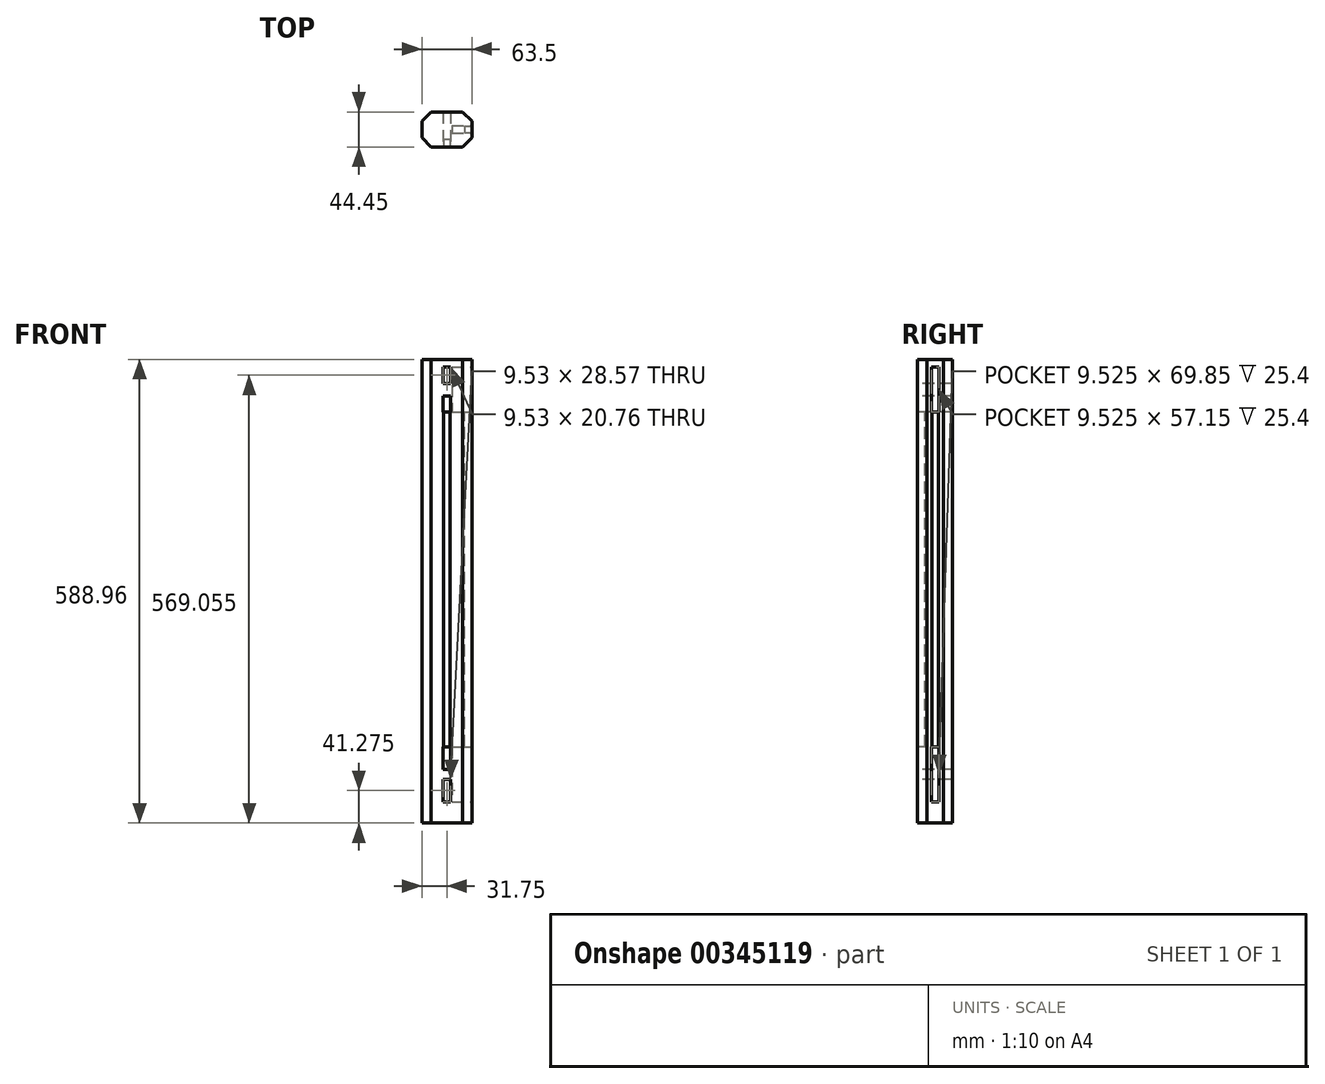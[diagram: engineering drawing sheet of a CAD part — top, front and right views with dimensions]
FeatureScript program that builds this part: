
annotation { "Feature Type Name" : "Feature", "Feature Type Description" : "" }
export const myFeature = defineFeature(function(context is Context, id is Id, definition is map)
    precondition{}
    {
        {
            var Q0;
            Q0=qCreatedBy(makeId("Top.planeOp"),FACE);
            var sketch = newSketch(context, id + "F0", { "sketchPlane" : qUnion([Q0])});
            skLineSegment(sketch, "E0", {"start": v(0, 0) * mm, "end": v(63.5, 0) * mm});
            skLineSegment(sketch, "E1", {"start": v(63.5, 0) * mm, "end": v(63.5, 44.45) * mm});
            skLineSegment(sketch, "E2", {"start": v(63.5, 44.45) * mm, "end": v(0, 44.45) * mm});
            skLineSegment(sketch, "E3", {"start": v(0, 44.45) * mm, "end": v(0, 0) * mm});
            skSolve(sketch);
        }
        {
            var Q0;
            Q0=qSketchRegion(id+"F0",true);
            extrude(context, id + "F1", {"entities" : qUnion([Q0]), "depth" : 588.96 * mm});
        }
        {
            var Q0;
            Q0=makeQuery(id+"F1.opExtrude","SWEPT_FACE",FACE,{"disambiguationData":[OSD([sQuery(id+"F0.wireOp",EDGE,"E1")])]});
            var sketch = newSketch(context, id + "F2", { "sketchPlane" : qUnion([Q0])});
            skLineSegment(sketch, "E4", {"start": v(17.46, 579.44) * mm, "end": v(17.46, 522.29) * mm});
            skLineSegment(sketch, "E5", {"start": v(17.46, 522.29) * mm, "end": v(26.99, 522.29) * mm});
            skLineSegment(sketch, "E6", {"start": v(26.99, 522.29) * mm, "end": v(26.99, 579.44) * mm});
            skLineSegment(sketch, "E7", {"start": v(26.99, 579.44) * mm, "end": v(17.46, 579.44) * mm});
            skLineSegment(sketch, "E8", {"start": v(17.46, 96.84) * mm, "end": v(17.46, 26.99) * mm});
            skLineSegment(sketch, "E9", {"start": v(17.46, 26.99) * mm, "end": v(26.99, 26.99) * mm});
            skLineSegment(sketch, "E10", {"start": v(26.99, 26.99) * mm, "end": v(26.99, 96.84) * mm});
            skLineSegment(sketch, "E11", {"start": v(26.99, 96.84) * mm, "end": v(17.46, 96.84) * mm});
            skPoint(sketch, "E12", {"position": v(18.26, 96.84) * mm});
            skPoint(sketch, "E13", {"position": v(26.2, 96.84) * mm});
            skPoint(sketch, "E14", {"position": v(18.26, 522.29) * mm});
            skPoint(sketch, "E15", {"position": v(26.2, 522.29) * mm});
            skLineSegment(sketch, "E16", {"start": v(18.26, 522.29) * mm, "end": v(18.26, 96.84) * mm});
            skLineSegment(sketch, "E17", {"start": v(26.2, 96.84) * mm, "end": v(26.2, 522.29) * mm});
            skSolve(sketch);
        }
        {
            var Q0;
            {var subQ4=sQuery(id+"F2.wireOp",EDGE,"E4");Q0=makeQuery(id+"F2.imprint","IMPRINT",FACE,{"disambiguationData":[TD([[makeQuery(id+"F2.imprint","IMPRINT",EDGE,{"derivedFrom":subQ4}),1.0]])]});}
            var Q1;
            {var subQ3=sQuery(id+"F2.wireOp",EDGE,"E8");Q1=makeQuery(id+"F2.imprint","IMPRINT",FACE,{"disambiguationData":[TD([[makeQuery(id+"F2.imprint","IMPRINT",EDGE,{"derivedFrom":subQ3}),1.0]])]});}
            extrude(context, id + "F3", {"entities" : qUnion([Q0, Q1]), "operationType" : NewBodyOperationType.REMOVE, "oppositeDirection" : true, "depth" : 25.4 * mm});
        }
        {
            var Q0;
            {var subQ0=sQuery(id+"F2.wireOp",EDGE,"E16");Q0=makeQuery(id+"F2.imprint","IMPRINT",FACE,{"disambiguationData":[TD([[makeQuery(id+"F2.imprint","IMPRINT",EDGE,{"derivedFrom":subQ0}),1.0]])]});}
            extrude(context, id + "F4", {"entities" : qUnion([Q0]), "operationType" : NewBodyOperationType.REMOVE, "oppositeDirection" : true, "depth" : 9.52 * mm});
        }
        {
            var Q0;
            Q0=makeQuery(id+"F1.opExtrude","SWEPT_FACE",FACE,{"disambiguationData":[OSD([sQuery(id+"F0.wireOp",EDGE,"E0")])]});
            var sketch = newSketch(context, id + "F5", { "sketchPlane" : qUnion([Q0])});
            skLineSegment(sketch, "E18", {"start": v(26.99, 579.44) * mm, "end": v(26.99, 558.67) * mm});
            skLineSegment(sketch, "E19", {"start": v(26.99, 558.67) * mm, "end": v(36.51, 558.67) * mm});
            skLineSegment(sketch, "E20", {"start": v(36.51, 558.67) * mm, "end": v(36.51, 579.44) * mm});
            skLineSegment(sketch, "E21", {"start": v(36.51, 579.44) * mm, "end": v(26.99, 579.44) * mm});
            skPoint(sketch, "E22.startSnap0", {"position": v(26.99, 569.06) * mm});
            skLineSegment(sketch, "E23", {"start": v(26.99, 55.56) * mm, "end": v(36.51, 55.56) * mm});
            skLineSegment(sketch, "E24", {"start": v(28.57, 522.03) * mm, "end": v(26.99, 522.03) * mm});
            skLineSegment(sketch, "E25", {"start": v(26.99, 522.03) * mm, "end": v(26.99, 522.03) * mm});
            skLineSegment(sketch, "E26", {"start": v(26.99, 522.03) * mm, "end": v(26.99, 542.8) * mm});
            skLineSegment(sketch, "E27", {"start": v(26.99, 542.8) * mm, "end": v(36.51, 542.8) * mm});
            skLineSegment(sketch, "E28", {"start": v(36.51, 542.8) * mm, "end": v(36.51, 522.03) * mm});
            skLineSegment(sketch, "E29", {"start": v(36.51, 522.03) * mm, "end": v(28.57, 522.03) * mm});
            skLineSegment(sketch, "E30", {"start": v(26.99, 55.56) * mm, "end": v(26.99, 55.56) * mm});
            skLineSegment(sketch, "E31", {"start": v(26.99, 55.56) * mm, "end": v(26.99, 26.99) * mm});
            skLineSegment(sketch, "E32", {"start": v(36.51, 55.56) * mm, "end": v(36.51, 26.99) * mm});
            skLineSegment(sketch, "E33", {"start": v(36.51, 26.99) * mm, "end": v(26.99, 26.99) * mm});
            skLineSegment(sketch, "E34", {"start": v(36.51, 68.26) * mm, "end": v(36.51, 96.84) * mm});
            skLineSegment(sketch, "E35", {"start": v(36.51, 96.84) * mm, "end": v(26.99, 96.84) * mm});
            skLineSegment(sketch, "E36", {"start": v(26.99, 96.84) * mm, "end": v(26.99, 68.26) * mm});
            skLineSegment(sketch, "E37", {"start": v(26.99, 68.26) * mm, "end": v(36.51, 68.26) * mm});
            skPoint(sketch, "E38", {"position": v(35.72, 96.84) * mm});
            skPoint(sketch, "E39", {"position": v(27.78, 96.84) * mm});
            skLineSegment(sketch, "E40", {"start": v(35.72, 96.84) * mm, "end": v(35.72, 522.03) * mm});
            skLineSegment(sketch, "E41", {"start": v(27.78, 96.84) * mm, "end": v(27.78, 522.03) * mm});
            skSolve(sketch);
        }
        {
            var Q0;
            {var subQ0=sQuery(id+"F5.wireOp",EDGE,"E40");Q0=makeQuery(id+"F5.imprint","IMPRINT",FACE,{"disambiguationData":[TD([[makeQuery(id+"F5.imprint","IMPRINT",EDGE,{"derivedFrom":subQ0}),1.0]])]});}
            extrude(context, id + "F6", {"entities" : qUnion([Q0]), "operationType" : NewBodyOperationType.REMOVE, "oppositeDirection" : true, "depth" : 9.52 * mm});
        }
        {
            var Q0;
            Q0=makeQuery(id+"F5.imprint","IMPRINT",FACE,{"disambiguationData":[TD([[makeQuery(id+"F5.imprint","IMPRINT",EDGE,{"derivedFrom":sQuery(id+"F5.wireOp",EDGE,"E18")}),1.0]])]});
            var Q1;
            {var subQ0=sQuery(id+"F5.wireOp",EDGE,"E26");Q1=makeQuery(id+"F5.imprint","IMPRINT",FACE,{"disambiguationData":[TD([[makeQuery(id+"F5.imprint","IMPRINT",EDGE,{"derivedFrom":subQ0}),-1.0]])]});}
            var Q2;
            {var subQ4=sQuery(id+"F5.wireOp",EDGE,"E34");Q2=makeQuery(id+"F5.imprint","IMPRINT",FACE,{"disambiguationData":[TD([[makeQuery(id+"F5.imprint","IMPRINT",EDGE,{"derivedFrom":subQ4}),1.0]])]});}
            var Q3;
            Q3=makeQuery(id+"F5.imprint","IMPRINT",FACE,{"disambiguationData":[TD([[makeQuery(id+"F5.imprint","IMPRINT",EDGE,{"derivedFrom":sQuery(id+"F5.wireOp",EDGE,"E23")}),-1.0]])]});
            extrude(context, id + "F7", {"entities" : qUnion([Q0, Q1, Q2, Q3]), "operationType" : NewBodyOperationType.REMOVE, "endBound" : BoundingType.THROUGH_ALL, "oppositeDirection" : true, "depth" : 25.4 * mm});
        }
        {
            var Q0;
            Q0=makeQuery(id+"F1.opExtrude","SWEPT_EDGE",EDGE,{"disambiguationData":[OSD([sQuery(id+"F0.wireOp",EDGE,"E1"),sQuery(id+"F0.wireOp",EDGE,"E2")])]});
            var Q1;
            Q1=makeQuery(id+"F1.opExtrude","SWEPT_EDGE",EDGE,{"disambiguationData":[OSD([sQuery(id+"F0.wireOp",EDGE,"E2"),sQuery(id+"F0.wireOp",EDGE,"E3")])]});
            var Q2;
            Q2=makeQuery(id+"F1.opExtrude","SWEPT_EDGE",EDGE,{"disambiguationData":[OSD([sQuery(id+"F0.wireOp",EDGE,"E0"),sQuery(id+"F0.wireOp",EDGE,"E1")])]});
            var Q3;
            Q3=makeQuery(id+"F1.opExtrude","SWEPT_EDGE",EDGE,{"disambiguationData":[OSD([sQuery(id+"F0.wireOp",EDGE,"E0"),sQuery(id+"F0.wireOp",EDGE,"E3")])]});
            chamfer(context, id + "F8", {"entities" : qUnion([Q0, Q1, Q2, Q3]), "width" : 11.9 * mm, "tangentPropagation" : true});
        }
    });
